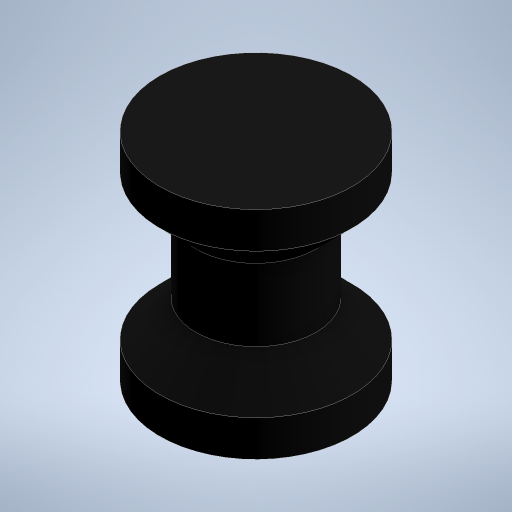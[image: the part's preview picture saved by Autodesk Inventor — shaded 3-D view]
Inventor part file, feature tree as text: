
AUTODESK INVENTOR PART (.ipt)
format: ipt  version: 2024.2 (Build 282272000, 272)  size: 239,616 bytes
history: native  units: mm
features: extrude x4, other x1, sketch x1, chamfer x1
ambient origin geometry x8: Origin, YZ Plane, XZ Plane, XY Plane, X Axis, Y Axis, Z Axis, Center Point
bodies: Body1 (feature_tree)
feature tree (7):
  other  "Bryła1"
  sketch  "Szkic1"
  extrude  "Wyciągnięcie proste1"  Depth=1.5mm
  extrude  "Wyciągnięcie proste2"  Depth=2.5mm
  extrude  "Wyciągnięcie proste3"  Depth=10.0mm
  extrude  "Wyciągnięcie proste4"  Depth=16.0mm
  chamfer  "Faza1"  Distance=18.0mm
